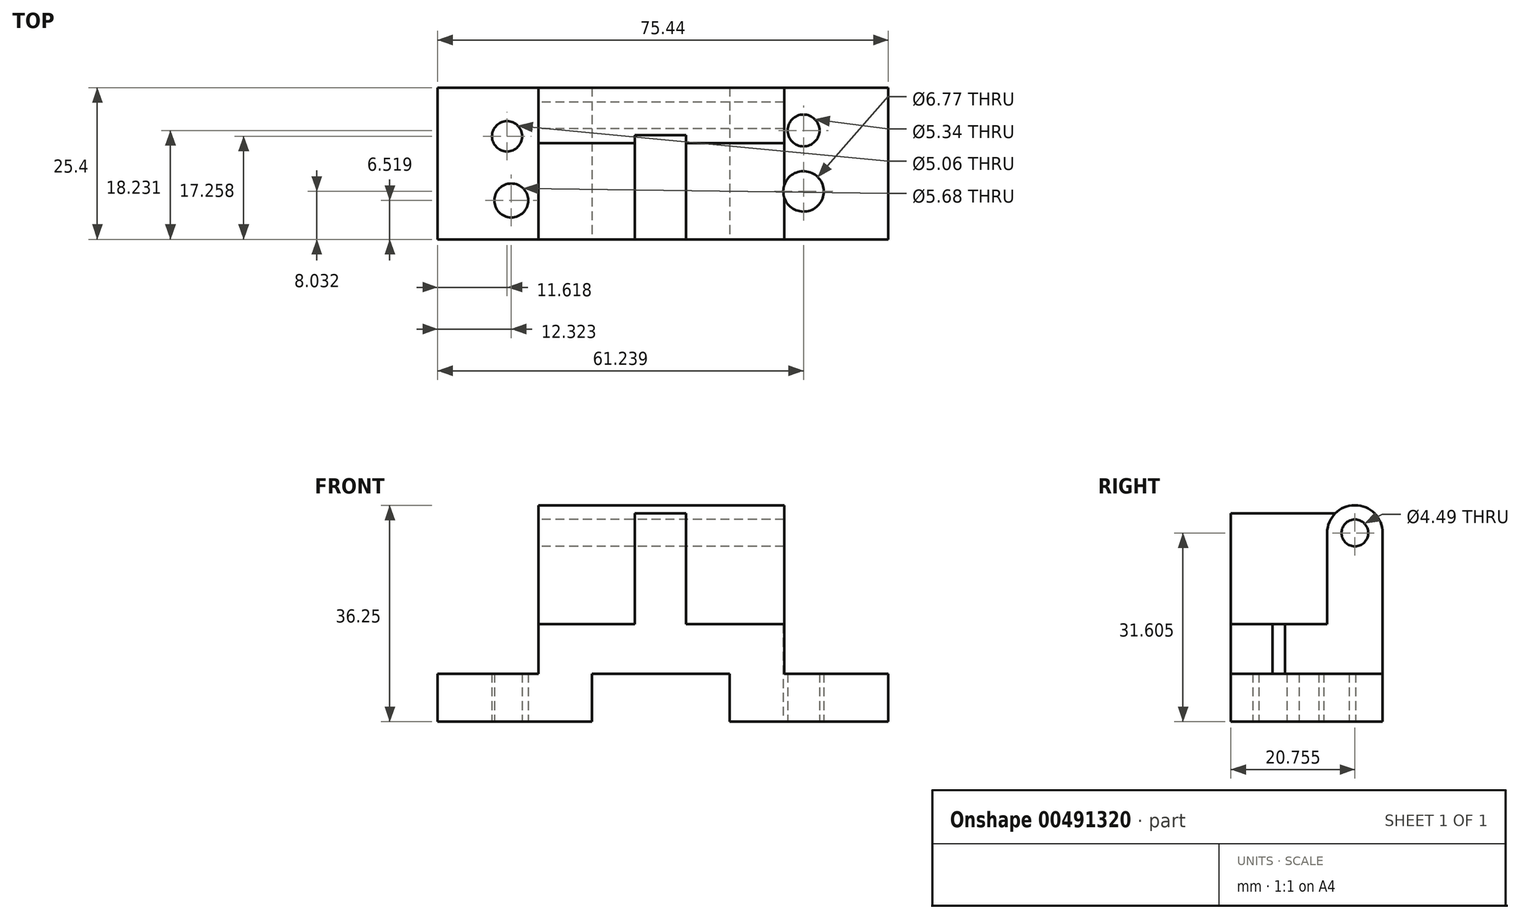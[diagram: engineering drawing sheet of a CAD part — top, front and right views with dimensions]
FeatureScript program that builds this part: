
annotation { "Feature Type Name" : "Feature", "Feature Type Description" : "" }
export const myFeature = defineFeature(function(context is Context, id is Id, definition is map)
    precondition{}
    {
        {
            var Q0;
            Q0=qCreatedBy(makeId("Front.planeOp"),FACE);
            var sketch = newSketch(context, id + "F0", { "sketchPlane" : qUnion([Q0])});
            skLineSegment(sketch, "E0", {"start": v(0, 0) * mm, "end": v(0, 8.06) * mm});
            skLineSegment(sketch, "E1", {"start": v(0, 8.06) * mm, "end": v(16.87, 8.06) * mm});
            skLineSegment(sketch, "E2", {"start": v(16.87, 8.06) * mm, "end": v(16.87, 16.33) * mm});
            skLineSegment(sketch, "E3", {"start": v(16.87, 16.33) * mm, "end": v(58.02, 16.33) * mm});
            skLineSegment(sketch, "E4", {"start": v(58.02, 16.33) * mm, "end": v(58.02, 8.06) * mm});
            skLineSegment(sketch, "E5", {"start": v(58.02, 8.06) * mm, "end": v(75.44, 8.06) * mm});
            skLineSegment(sketch, "E6", {"start": v(75.44, 8.06) * mm, "end": v(75.44, 0) * mm});
            skLineSegment(sketch, "E7", {"start": v(75.44, 0) * mm, "end": v(48.88, 0) * mm});
            skLineSegment(sketch, "E8", {"start": v(25.8, 8.06) * mm, "end": v(25.8, 0) * mm});
            skLineSegment(sketch, "E9", {"start": v(25.8, 8.06) * mm, "end": v(48.88, 8.06) * mm});
            skLineSegment(sketch, "E10", {"start": v(48.88, 8.06) * mm, "end": v(48.88, 0) * mm});
            skLineSegment(sketch, "E11.trimOffspring", {"start": v(25.8, 0) * mm, "end": v(0, 0) * mm});
            skSolve(sketch);
        }
        {
            var Q0;
            Q0 = qSketchRegion(id + "F0", true);
            extrude(context, id + "F1", {"entities" : qUnion([Q0]), "oppositeDirection" : true, "depth" : 25.4 * mm});
        }
        {
            var Q0;
            Q0=makeQuery(id+"F1.opExtrude","SWEPT_FACE",FACE,{"disambiguationData":[OSD([sQuery(id+"F0.wireOp",EDGE,"E11.trimOffspring")])]});
            var sketch = newSketch(context, id + "F2", { "sketchPlane" : qUnion([Q0])});
            skCircle(sketch, "E12", {"center": v(12.32, -6.52) * mm, "radius": 2.84 * mm});
            skCircle(sketch, "E13", {"center": v(11.62, -17.26) * mm, "radius": 2.53 * mm});
            skCircle(sketch, "E14", {"center": v(61.24, -8.03) * mm, "radius": 3.39 * mm});
            skCircle(sketch, "E15", {"center": v(61.24, -18.23) * mm, "radius": 2.67 * mm});
            skSolve(sketch);
        }
        {
            var Q0;
            Q0 = qSketchRegion(id + "F2", true);
            extrude(context, id + "F3", {"entities" : qUnion([Q0]), "operationType" : NewBodyOperationType.REMOVE, "oppositeDirection" : true, "depth" : 25.4 * mm});
        }
        {
            var Q0;
            Q0=makeQuery(id+"F1.opExtrude","SWEPT_FACE",FACE,{"disambiguationData":[OSD([sQuery(id+"F0.wireOp",EDGE,"E2")])]});
            var sketch = newSketch(context, id + "F4", { "sketchPlane" : qUnion([Q0])});
            skLineSegment(sketch, "E16.bottom", {"start": v(-25.4, 16.33) * mm, "end": v(-16.1, 16.33) * mm});
            skLineSegment(sketch, "E16.left", {"start": v(-25.4, 16.33) * mm, "end": v(-25.4, 31.6) * mm});
            skLineSegment(sketch, "E16.right", {"start": v(-16.1, 16.33) * mm, "end": v(-16.1, 31.6) * mm});
            skArc(sketch, "E17", {"start": v(-16.1, 31.6) * mm, "mid": v(-20.75, 36.25) * mm, "end": v(-25.4, 31.6) * mm});
            skCircle(sketch, "E18", {"center": v(-20.75, 31.6) * mm, "radius": 2.24 * mm});
            skSolve(sketch);
        }
        {
            var Q0;
            Q0 = qSketchRegion(id + "F4", true);
            extrude(context, id + "F5", {"entities" : qUnion([Q0]), "operationType" : NewBodyOperationType.ADD, "oppositeDirection" : true, "depth" : 41.15 * mm});
        }
        {
            var Q0;
            Q0=makeQuery(id+"F1.opExtrude","SWEPT_FACE",FACE,{"disambiguationData":[OSD([sQuery(id+"F0.wireOp",EDGE,"E3")])]});
            var sketch = newSketch(context, id + "F6", { "sketchPlane" : qUnion([Q0])});
            skLineSegment(sketch, "E19.bottom", {"start": v(41.6, 0) * mm, "end": v(33, 0) * mm});
            skLineSegment(sketch, "E19.top", {"start": v(41.6, 17.45) * mm, "end": v(33, 17.45) * mm});
            skLineSegment(sketch, "E19.left", {"start": v(41.6, 0) * mm, "end": v(41.6, 17.45) * mm});
            skLineSegment(sketch, "E19.right", {"start": v(33, 0) * mm, "end": v(33, 17.45) * mm});
            skSolve(sketch);
        }
        {
            var Q0;
            Q0 = qSketchRegion(id + "F6", true);
            extrude(context, id + "F7", {"entities" : qUnion([Q0]), "operationType" : NewBodyOperationType.ADD, "depth" : 18.54 * mm});
        }
    });
